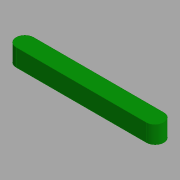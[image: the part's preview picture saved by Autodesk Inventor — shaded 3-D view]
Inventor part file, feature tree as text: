
AUTODESK INVENTOR PART (.ipt)
format: ipt  version: 2014 SP2 (Build 180246200, 246)  size: 126,464 bytes
history: native  units: mm
features: other x2, extrude x1
ambient origin geometry x8: Origin, YZ Plane, XZ Plane, XY Plane, X Axis, Y Axis, Z Axis, Center Point
bodies: Body1 (feature_tree)
feature tree (3):
  other  "Těleso1"
  extrude  "Vysunutí1"  Depth=2.0mm TaperAngle=0.0deg
  other  "Referenční1"
